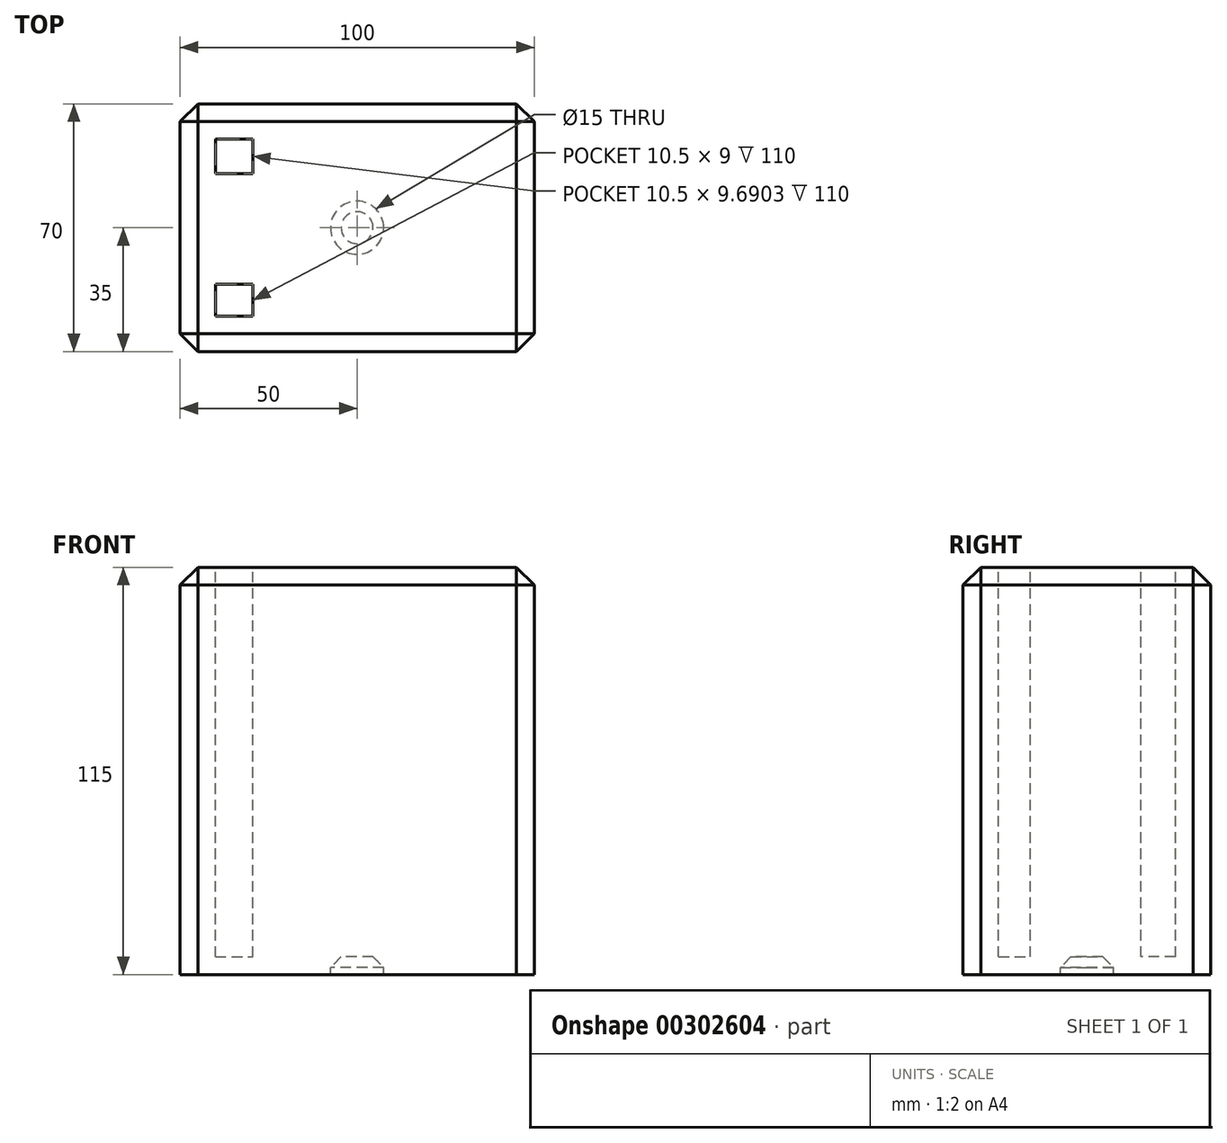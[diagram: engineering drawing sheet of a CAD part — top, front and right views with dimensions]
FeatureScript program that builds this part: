
annotation { "Feature Type Name" : "Feature", "Feature Type Description" : "" }
export const myFeature = defineFeature(function(context is Context, id is Id, definition is map)
    precondition{}
    {
        {
            var Q0;
            Q0=qCreatedBy(makeId("Top.planeOp"),FACE);
            var sketch = newSketch(context, id + "F0", { "sketchPlane" : qUnion([Q0])});
            skLineSegment(sketch, "E0.bottom", {"start": v(0, 0) * mm, "end": v(100, 0) * mm});
            skLineSegment(sketch, "E0.top", {"start": v(0, 70) * mm, "end": v(100, 70) * mm});
            skLineSegment(sketch, "E0.left", {"start": v(0, 0) * mm, "end": v(0, 70) * mm});
            skLineSegment(sketch, "E0.right", {"start": v(100, 0) * mm, "end": v(100, 70) * mm});
            skSolve(sketch);
        }
        {
            var Q0;
            Q0=makeQuery(id+"F0.imprint","IMPRINT",FACE,{"disambiguationData":[TD([[makeQuery(id+"F0.imprint","IMPRINT",EDGE,{"derivedFrom":sQuery(id+"F0.wireOp",EDGE,"E0.bottom")}),1.0]])]});
            extrude(context, id + "F1", {"entities" : qUnion([Q0]), "depth" : 115 * mm});
        }
        {
            var Q0;
            Q0=makeQuery(id+"F1.opExtrude","CAP_FACE",FACE,{"disambiguationData":[OSD([sQuery(id+"F0.wireOp",EDGE,"E0.bottom"),sQuery(id+"F0.wireOp",EDGE,"E0.top"),sQuery(id+"F0.wireOp",EDGE,"E0.left"),sQuery(id+"F0.wireOp",EDGE,"E0.right")])],"isStart":false});
            var sketch = newSketch(context, id + "F2", { "sketchPlane" : qUnion([Q0])});
            skLineSegment(sketch, "E1.bottom", {"start": v(10, 60) * mm, "end": v(90, 60) * mm});
            skLineSegment(sketch, "E1.top", {"start": v(10, 10) * mm, "end": v(90, 10) * mm});
            skLineSegment(sketch, "E1.left", {"start": v(10, 60) * mm, "end": v(10, 10) * mm});
            skLineSegment(sketch, "E1.right", {"start": v(90, 60) * mm, "end": v(90, 10) * mm});
            skLineSegment(sketch, "E2.bottom", {"start": v(10, 60) * mm, "end": v(20.5, 60) * mm});
            skLineSegment(sketch, "E2.top", {"start": v(10, 50.3) * mm, "end": v(20.5, 50.3) * mm});
            skLineSegment(sketch, "E2.left", {"start": v(10, 60) * mm, "end": v(10, 50.3) * mm});
            skLineSegment(sketch, "E2.right", {"start": v(20.5, 60) * mm, "end": v(20.5, 50.3) * mm});
            skLineSegment(sketch, "E3.bottom", {"start": v(90, 60) * mm, "end": v(79.5, 60) * mm});
            skLineSegment(sketch, "E3.top", {"start": v(90, 51) * mm, "end": v(79.5, 51) * mm});
            skLineSegment(sketch, "E3.left", {"start": v(90, 60) * mm, "end": v(90, 51) * mm});
            skLineSegment(sketch, "E3.right", {"start": v(79.5, 60) * mm, "end": v(79.5, 51) * mm});
            skLineSegment(sketch, "E4.bottom", {"start": v(10, 10) * mm, "end": v(20.5, 10) * mm});
            skLineSegment(sketch, "E4.top", {"start": v(10, 19) * mm, "end": v(20.5, 19) * mm});
            skLineSegment(sketch, "E4.left", {"start": v(10, 10) * mm, "end": v(10, 19) * mm});
            skLineSegment(sketch, "E4.right", {"start": v(20.5, 10) * mm, "end": v(20.5, 19) * mm});
            skLineSegment(sketch, "E5.bottom", {"start": v(90, 10) * mm, "end": v(79.5, 10) * mm});
            skLineSegment(sketch, "E5.top", {"start": v(90, 19.09) * mm, "end": v(79.5, 19.09) * mm});
            skLineSegment(sketch, "E5.left", {"start": v(90, 10) * mm, "end": v(90, 19.09) * mm});
            skLineSegment(sketch, "E5.right", {"start": v(79.5, 10) * mm, "end": v(79.5, 19.09) * mm});
            skLineSegment(sketch, "E6.bottom", {"start": v(20.5, 60) * mm, "end": v(79.5, 60) * mm});
            skLineSegment(sketch, "E6.top", {"start": v(20.5, 55.5) * mm, "end": v(79.5, 55.5) * mm});
            skLineSegment(sketch, "E6.left", {"start": v(20.5, 60) * mm, "end": v(20.5, 55.5) * mm});
            skLineSegment(sketch, "E6.right", {"start": v(79.5, 60) * mm, "end": v(79.5, 55.5) * mm});
            skPoint(sketch, "E7.oppositeSnap0", {"position": v(20.5, 14.5) * mm});
            skLineSegment(sketch, "E7.bottom", {"start": v(20.5, 10) * mm, "end": v(79.5, 10) * mm});
            skLineSegment(sketch, "E7.top", {"start": v(20.5, 14.5) * mm, "end": v(79.5, 14.5) * mm});
            skLineSegment(sketch, "E7.left", {"start": v(20.5, 10) * mm, "end": v(20.5, 14.5) * mm});
            skLineSegment(sketch, "E7.right", {"start": v(79.5, 10) * mm, "end": v(79.5, 14.5) * mm});
            skSolve(sketch);
        }
        {
            var Q0;
            Q0=makeQuery(id+"F2.imprint","IMPRINT",FACE,{"disambiguationData":[TD([[makeQuery(id+"F2.imprint","IMPRINT",EDGE,{"derivedFrom":sQuery(id+"F2.wireOp",EDGE,"E2.bottom")}),-1.0]])]});
            var Q1;
            Q1=makeQuery(id+"F2.imprint","IMPRINT",FACE,{"disambiguationData":[TD([[makeQuery(id+"F2.imprint","IMPRINT",EDGE,{"derivedFrom":sQuery(id+"F2.wireOp",EDGE,"E3.bottom")}),1.0]])]});
            var Q2;
            Q2=makeQuery(id+"F2.imprint","IMPRINT",FACE,{"disambiguationData":[TD([[makeQuery(id+"F2.imprint","IMPRINT",EDGE,{"derivedFrom":sQuery(id+"F2.wireOp",EDGE,"E4.bottom")}),1.0]])]});
            var Q3;
            Q3=makeQuery(id+"F2.imprint","IMPRINT",FACE,{"disambiguationData":[TD([[makeQuery(id+"F2.imprint","IMPRINT",EDGE,{"derivedFrom":sQuery(id+"F2.wireOp",EDGE,"E5.bottom")}),-1.0]])]});
            var Q4;
            Q4=makeQuery(id+"F2.imprint","IMPRINT",FACE,{"disambiguationData":[TD([[makeQuery(id+"F2.imprint","IMPRINT",EDGE,{"derivedFrom":sQuery(id+"F2.wireOp",EDGE,"E1.left")}),1.0]])]});
            extrude(context, id + "F3", {"entities" : qUnion([Q0, Q1, Q2, Q3, Q4]), "operationType" : NewBodyOperationType.REMOVE, "oppositeDirection" : true, "depth" : 110 * mm});
        }
        {
            var Q0;
            Q0=makeQuery(id+"F3.boolean.opBoolean","COPY",FACE,{"derivedFrom":makeQuery(id+"F3.opExtrude","CAP_FACE",FACE,{"disambiguationData":[OSD([sQuery(id+"F2.wireOp",EDGE,"E1.left"),sQuery(id+"F2.wireOp",EDGE,"E1.right"),sQuery(id+"F2.wireOp",EDGE,"E2.bottom"),sQuery(id+"F2.wireOp",EDGE,"E2.left"),sQuery(id+"F2.wireOp",EDGE,"E3.bottom"),sQuery(id+"F2.wireOp",EDGE,"E3.left"),sQuery(id+"F2.wireOp",EDGE,"E4.bottom"),sQuery(id+"F2.wireOp",EDGE,"E4.left"),sQuery(id+"F2.wireOp",EDGE,"E5.bottom"),sQuery(id+"F2.wireOp",EDGE,"E5.left"),sQuery(id+"F2.wireOp",EDGE,"E6.top"),sQuery(id+"F2.wireOp",EDGE,"E6.left"),sQuery(id+"F2.wireOp",EDGE,"E6.right"),sQuery(id+"F2.wireOp",EDGE,"E7.top"),sQuery(id+"F2.wireOp",EDGE,"E7.left"),sQuery(id+"F2.wireOp",EDGE,"E7.right")])],"isStart":false})});
            var sketch = newSketch(context, id + "F4", { "sketchPlane" : qUnion([Q0])});
            skCircle(sketch, "E8", {"center": v(50, 35) * mm, "radius": 7.5 * mm});
            skSolve(sketch);
        }
        {
            var Q0;
            Q0 = qSketchRegion(id + "F4", true);
            extrude(context, id + "F5", {"entities" : qUnion([Q0]), "operationType" : NewBodyOperationType.REMOVE, "oppositeDirection" : true, "depth" : 25 * mm});
        }
        {
            var Q0;
            Q0=makeQuery(id+"F5.boolean.opBoolean","COPY",EDGE,{"derivedFrom":makeQuery(id+"F5.opExtrude","CAP_EDGE",EDGE,{"disambiguationData":[OSD([sQuery(id+"F4.wireOp",EDGE,"E8")])],"isStart":true})});
            chamfer(context, id + "F6", {"entities" : qUnion([Q0]), "width" : 3 * mm, "tangentPropagation" : true});
        }
        {
            var Q0;
            Q0=makeQuery(id+"F1.opExtrude","CAP_EDGE",EDGE,{"disambiguationData":[OSD([sQuery(id+"F0.wireOp",EDGE,"E0.left")])],"isStart":false});
            var Q1;
            Q1=makeQuery(id+"F1.opExtrude","CAP_EDGE",EDGE,{"disambiguationData":[OSD([sQuery(id+"F0.wireOp",EDGE,"E0.bottom")])],"isStart":false});
            var Q2;
            Q2=makeQuery(id+"F1.opExtrude","CAP_EDGE",EDGE,{"disambiguationData":[OSD([sQuery(id+"F0.wireOp",EDGE,"E0.right")])],"isStart":false});
            var Q3;
            Q3=makeQuery(id+"F1.opExtrude","CAP_EDGE",EDGE,{"disambiguationData":[OSD([sQuery(id+"F0.wireOp",EDGE,"E0.top")])],"isStart":false});
            var Q4;
            Q4=makeQuery(id+"F1.opExtrude","SWEPT_EDGE",EDGE,{"disambiguationData":[OSD([sQuery(id+"F0.wireOp",EDGE,"E0.bottom"),sQuery(id+"F0.wireOp",EDGE,"E0.right")])]});
            var Q5;
            Q5=makeQuery(id+"F1.opExtrude","SWEPT_EDGE",EDGE,{"disambiguationData":[OSD([sQuery(id+"F0.wireOp",EDGE,"E0.top"),sQuery(id+"F0.wireOp",EDGE,"E0.right")])]});
            var Q6;
            Q6=makeQuery(id+"F1.opExtrude","SWEPT_EDGE",EDGE,{"disambiguationData":[OSD([sQuery(id+"F0.wireOp",EDGE,"E0.top"),sQuery(id+"F0.wireOp",EDGE,"E0.left")])]});
            var Q7;
            Q7=makeQuery(id+"F1.opExtrude","SWEPT_EDGE",EDGE,{"disambiguationData":[OSD([sQuery(id+"F0.wireOp",EDGE,"E0.bottom"),sQuery(id+"F0.wireOp",EDGE,"E0.left")])]});
            chamfer(context, id + "F7", {"entities" : qUnion([Q0, Q1, Q2, Q3, Q4, Q5, Q6, Q7]), "width" : 5 * mm, "tangentPropagation" : true});
        }
    });
